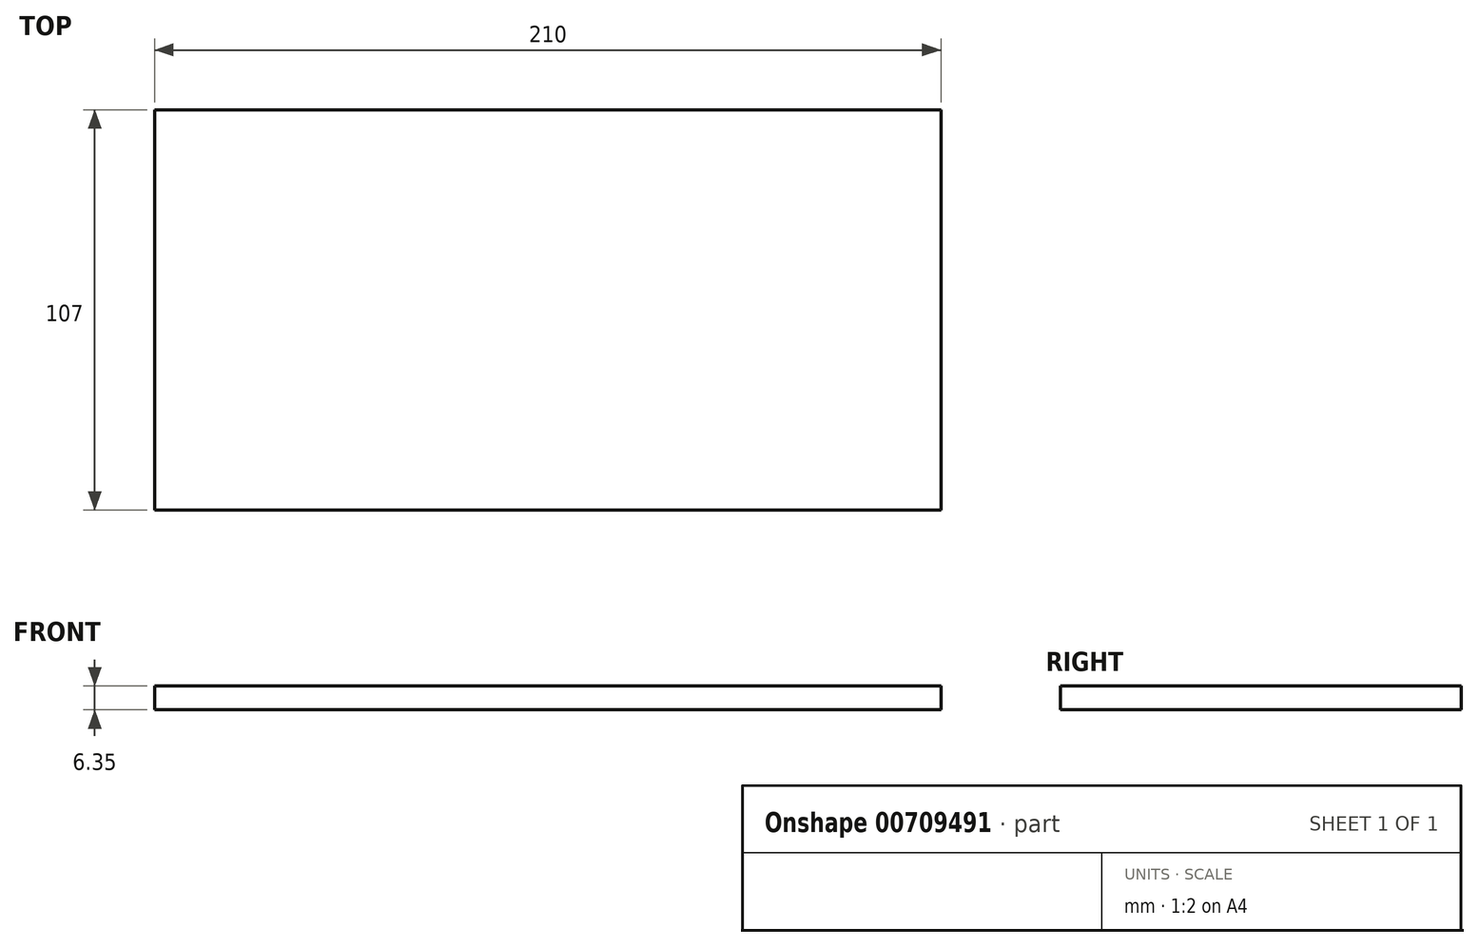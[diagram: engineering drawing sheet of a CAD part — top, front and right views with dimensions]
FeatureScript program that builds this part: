
annotation { "Feature Type Name" : "Feature", "Feature Type Description" : "" }
export const myFeature = defineFeature(function(context is Context, id is Id, definition is map)
    precondition{}
    {
        {
            var Q0;
            Q0=qCreatedBy(makeId("Top.planeOp"),FACE);
            var sketch = newSketch(context, id + "F0", { "sketchPlane" : qUnion([Q0])});
            skLineSegment(sketch, "E0.bottom", {"start": v(0, 0) * mm, "end": v(210, 0) * mm});
            skLineSegment(sketch, "E0.top", {"start": v(0, -107) * mm, "end": v(210, -107) * mm});
            skLineSegment(sketch, "E0.left", {"start": v(0, 0) * mm, "end": v(0, -107) * mm});
            skLineSegment(sketch, "E0.right", {"start": v(210, 0) * mm, "end": v(210, -107) * mm});
            skSolve(sketch);
        }
        {
            var Q0;
            Q0=makeQuery(id+"F0.imprint","IMPRINT",FACE,{"disambiguationData":[TD([[makeQuery(id+"F0.imprint","IMPRINT",EDGE,{"derivedFrom":sQuery(id+"F0.wireOp",EDGE,"E0.bottom")}),-1.0]])]});
            extrude(context, id + "F1", {"entities" : qUnion([Q0]), "depth" : 6.35 * mm, "offsetDistance" : 25.4 * mm});
        }
    });
